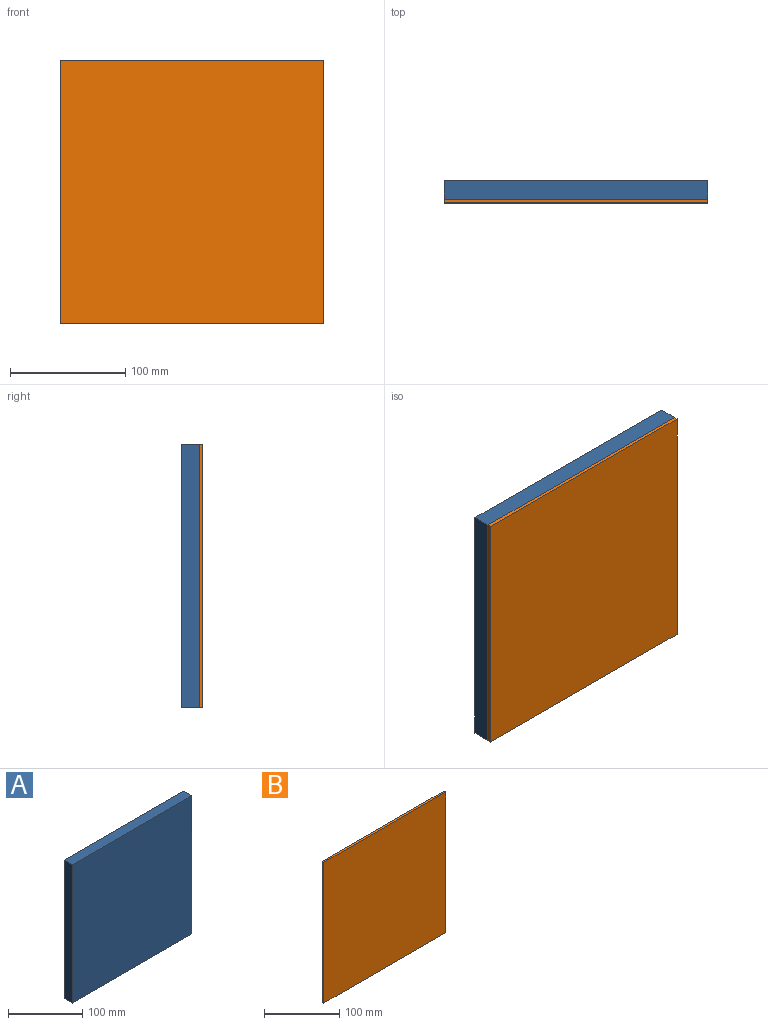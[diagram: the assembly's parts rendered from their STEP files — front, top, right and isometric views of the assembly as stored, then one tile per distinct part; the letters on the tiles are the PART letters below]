
ASSEMBLY  parts=2 mates=1
PART A: 6 faces, bbox 228.6x15.9x228.6 mm
  f0: plane 228.6x15.88mm, normal (0,0,-1), area 3629mm2, adj f1,f3,f4,f5
  f1: plane 228.6x15.88mm, normal (1,0,0), area 3629mm2, adj f0,f2,f4,f5
  f2: plane 228.6x15.88mm, normal (0,0,1), area 3629mm2, adj f1,f3,f4,f5
  f3: plane 228.6x15.88mm, normal (-1,0,0), area 3629mm2, adj f0,f2,f4,f5
  f4: plane 228.6x228.6mm, normal (0,-1,0), area 52258mm2, adj f0,f1,f2,f3
  f5: plane 228.6x228.6mm, normal (0,1,0), area 52258mm2, adj f0,f1,f2,f3
PART B: 6 faces, bbox 228.6x3.2x228.6 mm
  f0: plane 228.6x3.18mm, normal (0,0,-1), area 725.8mm2, adj f1,f3,f4,f5
  f1: plane 228.6x3.18mm, normal (1,0,0), area 725.8mm2, adj f0,f2,f4,f5
  f2: plane 228.6x3.18mm, normal (0,0,1), area 725.8mm2, adj f1,f3,f4,f5
  f3: plane 228.6x3.18mm, normal (-1,0,0), area 725.8mm2, adj f0,f2,f4,f5
  f4: plane 228.6x228.6mm, normal (0,-1,0), area 52258mm2, adj f0,f1,f2,f3
  f5: plane 228.6x228.6mm, normal (0,1,0), area 52258mm2, adj f0,f1,f2,f3
PLACE A t=(614.56,24.65,623.47)mm
PLACE B t=(598.22,8.78,623.47)mm
MATE fastened B.f5 <-> A.f4  axis (0,1,0) through (5.18,8.78,20.59)mm
